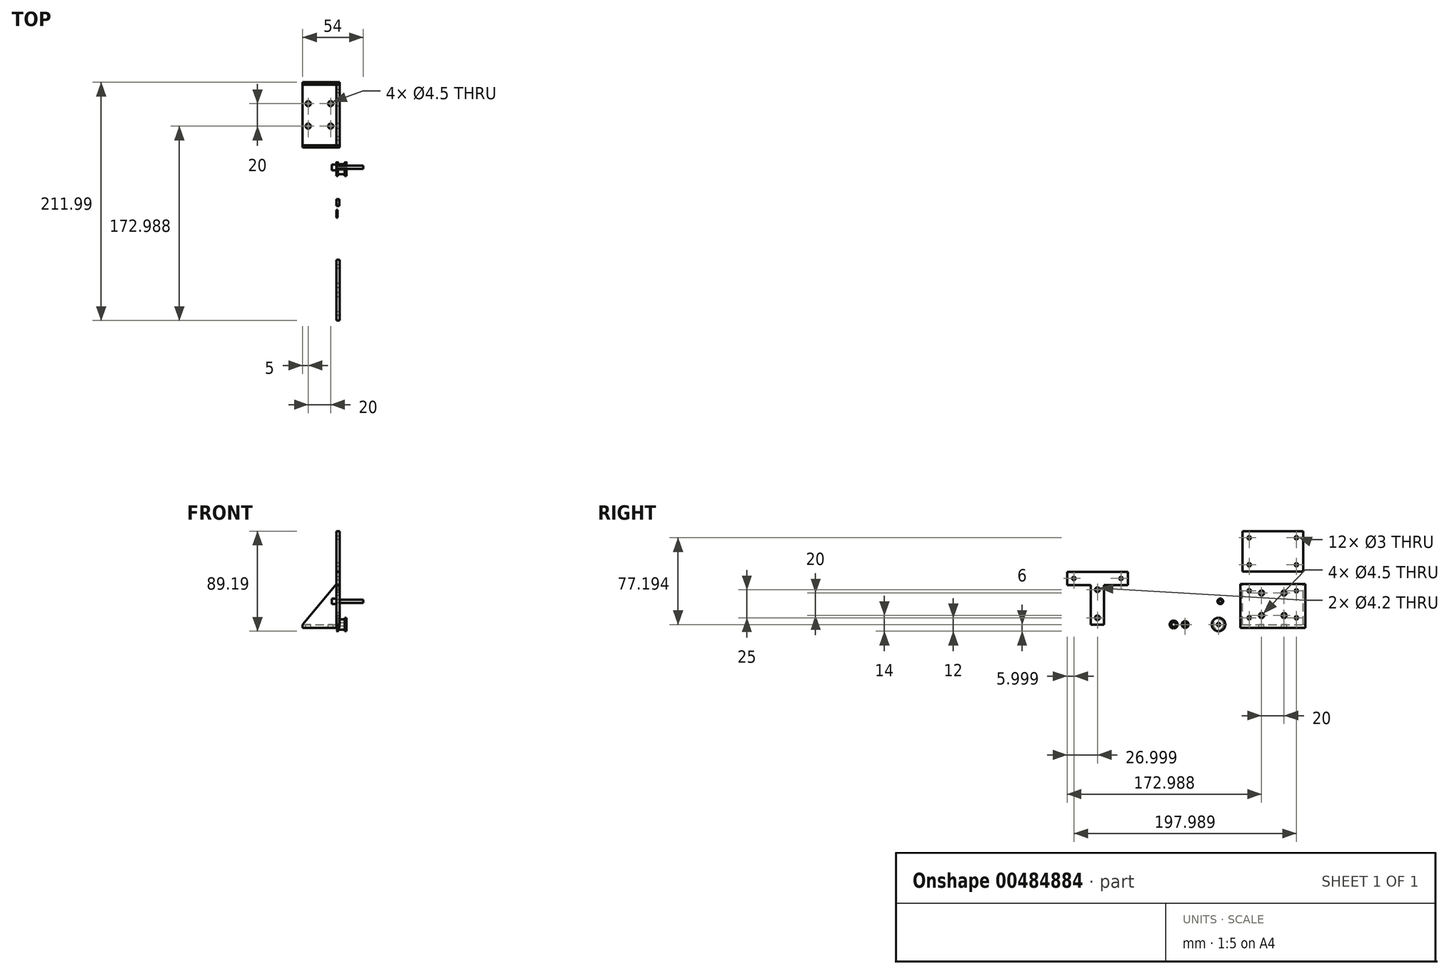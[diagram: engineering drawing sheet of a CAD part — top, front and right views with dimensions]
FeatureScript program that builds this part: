
annotation { "Feature Type Name" : "Feature", "Feature Type Description" : "" }
export const myFeature = defineFeature(function(context is Context, id is Id, definition is map)
    precondition{}
    {
        {
            var Q0;
            Q0=qCreatedBy(makeId("Right.planeOp"),FACE);
            var sketch = newSketch(context, id + "F0", { "sketchPlane" : qUnion([Q0])});
            skCircle(sketch, "E0", {"center": v(0, 0) * mm, "radius": 1.5 * mm});
            skCircle(sketch, "E1", {"center": v(0, 0) * mm, "radius": 4.5 * mm});
            skCircle(sketch, "E2", {"center": v(0, 0) * mm, "radius": 6 * mm});
            skSolve(sketch);
        }
        {
            var Q0;
            Q0=makeQuery(id+"F0.imprint","IMPRINT",FACE,{"disambiguationData":[TD([[makeQuery(id+"F0.imprint","IMPRINT",EDGE,{"derivedFrom":sQuery(id+"F0.wireOp",EDGE,"E0")}),1.0]])]});
            var Q1;
            Q1=makeQuery(id+"F0.imprint","IMPRINT",FACE,{"disambiguationData":[TD([[makeQuery(id+"F0.imprint","IMPRINT",EDGE,{"derivedFrom":sQuery(id+"F0.wireOp",EDGE,"E0")}),-1.0]])]});
            var Q2;
            Q2=makeQuery(id+"F0.imprint","IMPRINT",FACE,{"disambiguationData":[TD([[makeQuery(id+"F0.imprint","IMPRINT",EDGE,{"derivedFrom":sQuery(id+"F0.wireOp",EDGE,"E1")}),-1.0]])]});
            extrude(context, id + "F1", {"entities" : qUnion([Q0, Q1, Q2]), "depth" : 1.5 * mm, "offsetDistance" : 25 * mm});
        }
        {
            var Q0;
            Q0=makeQuery(id+"F0.imprint","IMPRINT",FACE,{"disambiguationData":[TD([[makeQuery(id+"F0.imprint","IMPRINT",EDGE,{"derivedFrom":sQuery(id+"F0.wireOp",EDGE,"E0")}),1.0]])]});
            var Q1;
            Q1=makeQuery(id+"F0.imprint","IMPRINT",FACE,{"disambiguationData":[TD([[makeQuery(id+"F0.imprint","IMPRINT",EDGE,{"derivedFrom":sQuery(id+"F0.wireOp",EDGE,"E0")}),-1.0]])]});
            extrude(context, id + "F2", {"entities" : qUnion([Q0, Q1]), "operationType" : NewBodyOperationType.ADD, "depth" : 7.5 * mm, "offsetDistance" : 25 * mm});
        }
        {
            var Q0;
            Q0=makeQuery(id+"F2.opExtrude","CAP_FACE",FACE,{"disambiguationData":[OSD([sQuery(id+"F0.wireOp",EDGE,"E1")])],"isStart":false});
            var sketch = newSketch(context, id + "F3", { "sketchPlane" : qUnion([Q0])});
            skCircle(sketch, "E3", {"center": v(0, 0) * mm, "radius": 6 * mm});
            skSolve(sketch);
        }
        {
            var Q0;
            Q0=makeQuery(id+"F3.imprint","IMPRINT",FACE,{"disambiguationData":[TD([[makeQuery(id+"F3.imprint","IMPRINT",EDGE,{"derivedFrom":makeQuery(id+"F2.opExtrude","CAP_EDGE",EDGE,{"disambiguationData":[OSD([sQuery(id+"F0.wireOp",EDGE,"E1")])],"isStart":false})}),1.0]])]});
            var Q1;
            Q1=makeQuery(id+"F3.imprint","IMPRINT",FACE,{"disambiguationData":[TD([[makeQuery(id+"F3.imprint","IMPRINT",EDGE,{"derivedFrom":sQuery(id+"F3.wireOp",EDGE,"E3")}),1.0]])]});
            extrude(context, id + "F4", {"entities" : qUnion([Q0, Q1]), "operationType" : NewBodyOperationType.ADD, "depth" : 1.5 * mm, "offsetDistance" : 25 * mm});
        }
        {
            var Q0;
            Q0=makeQuery(id+"F0.imprint","IMPRINT",FACE,{"disambiguationData":[TD([[makeQuery(id+"F0.imprint","IMPRINT",EDGE,{"derivedFrom":sQuery(id+"F0.wireOp",EDGE,"E0")}),1.0]])]});
            extrude(context, id + "F5", {"entities" : qUnion([Q0]), "operationType" : NewBodyOperationType.REMOVE, "endBound" : BoundingType.UP_TO_NEXT, "depth" : 25 * mm, "offsetDistance" : 25 * mm});
        }
        {
            var Q0;
            Q0=qCreatedBy(makeId("Right.planeOp"),FACE);
            var sketch = newSketch(context, id + "F6", { "sketchPlane" : qUnion([Q0])});
            skLineSegment(sketch, "E4.bottom", {"start": v(21.28, 0) * mm, "end": v(75.28, 0) * mm});
            skLineSegment(sketch, "E4.top", {"start": v(21.28, 36) * mm, "end": v(75.28, 36) * mm});
            skLineSegment(sketch, "E4.left", {"start": v(21.28, 0) * mm, "end": v(21.28, 36) * mm});
            skLineSegment(sketch, "E4.right", {"start": v(75.28, 0) * mm, "end": v(75.28, 36) * mm});
            skLineSegment(sketch, "E5", {"start": v(27.28, 0) * mm, "end": v(27.28, 6) * mm, "construction": true});
            skLineSegment(sketch, "E6", {"start": v(27.28, 6) * mm, "end": v(21.28, 6) * mm, "construction": true});
            skCircle(sketch, "E7", {"center": v(27.28, 6) * mm, "radius": 1.5 * mm});
            skLineSegment(sketch, "E8", {"start": v(27.28, 36) * mm, "end": v(27.28, 30) * mm, "construction": true});
            skLineSegment(sketch, "E9", {"start": v(27.28, 30) * mm, "end": v(21.28, 30) * mm, "construction": true});
            skLineSegment(sketch, "E10", {"start": v(69.28, 36) * mm, "end": v(69.28, 30) * mm, "construction": true});
            skLineSegment(sketch, "E11", {"start": v(69.28, 30) * mm, "end": v(75.28, 30) * mm, "construction": true});
            skLineSegment(sketch, "E12", {"start": v(75.28, 6) * mm, "end": v(69.28, 6) * mm, "construction": true});
            skLineSegment(sketch, "E13", {"start": v(69.28, 6) * mm, "end": v(69.28, 0) * mm, "construction": true});
            skCircle(sketch, "E14", {"center": v(69.28, 6) * mm, "radius": 1.5 * mm});
            skCircle(sketch, "E15", {"center": v(69.28, 30) * mm, "radius": 1.5 * mm});
            skCircle(sketch, "E16", {"center": v(27.28, 30) * mm, "radius": 1.5 * mm});
            skLineSegment(sketch, "E17", {"start": v(27.28, 30) * mm, "end": v(69.28, 30) * mm, "construction": true});
            skLineSegment(sketch, "E18", {"start": v(69.28, 30) * mm, "end": v(69.28, 6) * mm, "construction": true});
            skLineSegment(sketch, "E19", {"start": v(48.28, 36) * mm, "end": v(48.28, 0) * mm, "construction": true});
            skLineSegment(sketch, "E20", {"start": v(48.28, 18) * mm, "end": v(58.28, 18) * mm, "construction": true});
            skLineSegment(sketch, "E21", {"start": v(58.28, 18) * mm, "end": v(58.28, 28) * mm, "construction": true});
            skLineSegment(sketch, "E22", {"start": v(58.28, 18) * mm, "end": v(58.28, 8) * mm, "construction": true});
            skLineSegment(sketch, "E23", {"start": v(58.28, 28) * mm, "end": v(38.28, 28) * mm, "construction": true});
            skLineSegment(sketch, "E24", {"start": v(58.28, 8) * mm, "end": v(38.28, 8) * mm, "construction": true});
            skCircle(sketch, "E25", {"center": v(38.28, 28) * mm, "radius": 2.25 * mm});
            skCircle(sketch, "E26", {"center": v(58.28, 28) * mm, "radius": 2.25 * mm});
            skCircle(sketch, "E27", {"center": v(58.28, 8) * mm, "radius": 2.25 * mm});
            skCircle(sketch, "E28", {"center": v(38.28, 8) * mm, "radius": 2.25 * mm});
            skLineSegment(sketch, "E29", {"start": v(75.28, 36) * mm, "end": v(75.28, 47.2) * mm});
            skLineSegment(sketch, "E30.bottom", {"start": v(75.28, 47.2) * mm, "end": v(21.28, 47.2) * mm});
            skLineSegment(sketch, "E30.top", {"start": v(75.28, 83.2) * mm, "end": v(21.28, 83.2) * mm});
            skLineSegment(sketch, "E30.left", {"start": v(75.28, 47.2) * mm, "end": v(75.28, 83.2) * mm});
            skLineSegment(sketch, "E30.right", {"start": v(21.28, 47.2) * mm, "end": v(21.28, 83.2) * mm});
            skLineSegment(sketch, "E31", {"start": v(21.28, 53.2) * mm, "end": v(27.28, 53.2) * mm, "construction": true});
            skLineSegment(sketch, "E32", {"start": v(27.28, 53.2) * mm, "end": v(27.28, 47.2) * mm, "construction": true});
            skLineSegment(sketch, "E33", {"start": v(69.28, 47.2) * mm, "end": v(69.28, 53.2) * mm, "construction": true});
            skLineSegment(sketch, "E34", {"start": v(69.28, 53.2) * mm, "end": v(75.28, 53.2) * mm, "construction": true});
            skLineSegment(sketch, "E35", {"start": v(69.28, 83.2) * mm, "end": v(69.28, 77.2) * mm, "construction": true});
            skLineSegment(sketch, "E36", {"start": v(69.28, 77.2) * mm, "end": v(75.28, 77.2) * mm, "construction": true});
            skLineSegment(sketch, "E37", {"start": v(27.28, 83.2) * mm, "end": v(27.28, 77.2) * mm, "construction": true});
            skLineSegment(sketch, "E38", {"start": v(27.28, 77.2) * mm, "end": v(21.28, 77.2) * mm, "construction": true});
            skCircle(sketch, "E39", {"center": v(69.28, 77.2) * mm, "radius": 1.5 * mm});
            skCircle(sketch, "E40", {"center": v(69.28, 53.2) * mm, "radius": 1.5 * mm});
            skCircle(sketch, "E41", {"center": v(27.28, 53.2) * mm, "radius": 1.5 * mm});
            skCircle(sketch, "E42", {"center": v(27.28, 77.2) * mm, "radius": 1.5 * mm});
            skLineSegment(sketch, "E43", {"start": v(75.28, 0) * mm, "end": v(75.28, -3) * mm});
            skLineSegment(sketch, "E44", {"start": v(75.28, -3) * mm, "end": v(21.28, -3) * mm});
            skLineSegment(sketch, "E45", {"start": v(21.28, -3) * mm, "end": v(21.28, 0) * mm});
            skSolve(sketch);
        }
        {
            var Q0;
            {var subQ0=sQuery(id+"F6.wireOp",EDGE,"E4.bottom");Q0=makeQuery(id+"F6.imprint","IMPRINT",FACE,{"disambiguationData":[TD([[makeQuery(id+"F6.imprint","IMPRINT",EDGE,{"derivedFrom":subQ0}),1.0]])]});}
            var Q1;
            {var subQ0=sQuery(id+"F6.wireOp",EDGE,"E4.top");Q1=makeQuery(id+"F6.imprint","IMPRINT",FACE,{"disambiguationData":[TD([[makeQuery(id+"F6.imprint","IMPRINT",EDGE,{"derivedFrom":subQ0}),-1.0]])]});}
            var Q2;
            Q2=makeQuery(id+"F6.imprint","IMPRINT",FACE,{"disambiguationData":[TD([[makeQuery(id+"F6.imprint","IMPRINT",EDGE,{"derivedFrom":sQuery(id+"F6.wireOp",EDGE,"E4.bottom")}),-1.0]])]});
            extrude(context, id + "F7", {"entities" : qUnion([Q0, Q1, Q2]), "depth" : 3 * mm, "offsetDistance" : 25 * mm});
        }
        {
            var Q0;
            Q0=qCreatedBy(makeId("Right.planeOp"),FACE);
            var sketch = newSketch(context, id + "F8", { "sketchPlane" : qUnion([Q0])});
            skCircle(sketch, "E46", {"center": v(1.57, 20.62) * mm, "radius": 1.5 * mm});
            skCircle(sketch, "E47", {"center": v(1.57, 20.62) * mm, "radius": 2.5 * mm});
            skSolve(sketch);
        }
        {
            var Q0;
            Q0=makeQuery(id+"F8.imprint","IMPRINT",FACE,{"disambiguationData":[TD([[makeQuery(id+"F8.imprint","IMPRINT",EDGE,{"derivedFrom":sQuery(id+"F8.wireOp",EDGE,"E46")}),1.0]])]});
            extrude(context, id + "F9", {"entities" : qUnion([Q0]), "depth" : 24 * mm, "offsetDistance" : 25 * mm});
        }
        {
            var Q0;
            Q0=makeQuery(id+"F8.imprint","IMPRINT",FACE,{"disambiguationData":[TD([[makeQuery(id+"F8.imprint","IMPRINT",EDGE,{"derivedFrom":sQuery(id+"F8.wireOp",EDGE,"E46")}),-1.0]])]});
            var Q1;
            Q1=makeQuery(id+"F8.imprint","IMPRINT",FACE,{"disambiguationData":[TD([[makeQuery(id+"F8.imprint","IMPRINT",EDGE,{"derivedFrom":sQuery(id+"F8.wireOp",EDGE,"E46")}),1.0]])]});
            extrude(context, id + "F10", {"entities" : qUnion([Q0, Q1]), "operationType" : NewBodyOperationType.ADD, "oppositeDirection" : true, "depth" : 4 * mm, "offsetDistance" : 25 * mm});
        }
        {
            var Q0;
            Q0=qCreatedBy(makeId("Right.planeOp"),FACE);
            var sketch = newSketch(context, id + "F11", { "sketchPlane" : qUnion([Q0])});
            skCircle(sketch, "E48", {"center": v(-29.72, 0) * mm, "radius": 1.5 * mm});
            skCircle(sketch, "E49", {"center": v(-29.72, 0) * mm, "radius": 3 * mm});
            skCircle(sketch, "E50", {"center": v(-39.93, 0) * mm, "radius": 2 * mm});
            skCircle(sketch, "E51", {"center": v(-39.93, 0) * mm, "radius": 3.5 * mm});
            skSolve(sketch);
        }
        {
            var Q0;
            Q0=makeQuery(id+"F11.imprint","IMPRINT",FACE,{"disambiguationData":[TD([[makeQuery(id+"F11.imprint","IMPRINT",EDGE,{"derivedFrom":sQuery(id+"F11.wireOp",EDGE,"E48")}),-1.0]])]});
            extrude(context, id + "F12", {"entities" : qUnion([Q0]), "depth" : 2.5 * mm, "offsetDistance" : 25 * mm});
        }
        {
            var Q0;
            Q0=makeQuery(id+"F6.imprint","IMPRINT",FACE,{"disambiguationData":[TD([[makeQuery(id+"F6.imprint","IMPRINT",EDGE,{"derivedFrom":sQuery(id+"F6.wireOp",EDGE,"E30.bottom")}),-1.0]])]});
            extrude(context, id + "F13", {"entities" : qUnion([Q0]), "depth" : 3 * mm, "offsetDistance" : 25 * mm});
        }
        {
            var Q0;
            Q0=makeQuery(id+"F6.imprint","IMPRINT",FACE,{"disambiguationData":[TD([[makeQuery(id+"F6.imprint","IMPRINT",EDGE,{"derivedFrom":sQuery(id+"F6.wireOp",EDGE,"E4.bottom")}),-1.0]])]});
            extrude(context, id + "F14", {"entities" : qUnion([Q0]), "operationType" : NewBodyOperationType.ADD, "oppositeDirection" : true, "depth" : 30 * mm, "offsetDistance" : 25 * mm});
        }
        {
            var Q0;
            Q0=makeQuery(id+"F14.opExtrude","SWEPT_FACE",FACE,{"disambiguationData":[OSD([sQuery(id+"F6.wireOp",EDGE,"E4.bottom")])]});
            var sketch = newSketch(context, id + "F15", { "sketchPlane" : qUnion([Q0])});
            skLineSegment(sketch, "E52", {"start": v(-15, 21.28) * mm, "end": v(-15, 75.28) * mm});
            skLineSegment(sketch, "E53.bottom", {"start": v(-25, 58.28) * mm, "end": v(-5, 58.28) * mm, "construction": true});
            skLineSegment(sketch, "E53.top", {"start": v(-25, 38.28) * mm, "end": v(-5, 38.28) * mm, "construction": true});
            skLineSegment(sketch, "E53.left", {"start": v(-25, 58.28) * mm, "end": v(-25, 38.28) * mm, "construction": true});
            skLineSegment(sketch, "E53.right", {"start": v(-5, 58.28) * mm, "end": v(-5, 38.28) * mm, "construction": true});
            skPoint(sketch, "E53.middle", {"position": v(-15, 48.28) * mm});
            skCircle(sketch, "E54", {"center": v(-5, 38.28) * mm, "radius": 2.25 * mm});
            skCircle(sketch, "E55", {"center": v(-25, 38.28) * mm, "radius": 2.25 * mm});
            skCircle(sketch, "E56", {"center": v(-25, 58.28) * mm, "radius": 2.25 * mm});
            skCircle(sketch, "E57", {"center": v(-5, 58.28) * mm, "radius": 2.25 * mm});
            skSolve(sketch);
        }
        {
            var Q0;
            Q0=makeQuery(id+"F15.imprint","IMPRINT",FACE,{"disambiguationData":[TD([[makeQuery(id+"F15.imprint","IMPRINT",EDGE,{"derivedFrom":sQuery(id+"F15.wireOp",EDGE,"E55")}),1.0]])]});
            var Q1;
            Q1=makeQuery(id+"F15.imprint","IMPRINT",FACE,{"disambiguationData":[TD([[makeQuery(id+"F15.imprint","IMPRINT",EDGE,{"derivedFrom":sQuery(id+"F15.wireOp",EDGE,"E54")}),1.0]])]});
            var Q2;
            Q2=makeQuery(id+"F15.imprint","IMPRINT",FACE,{"disambiguationData":[TD([[makeQuery(id+"F15.imprint","IMPRINT",EDGE,{"derivedFrom":sQuery(id+"F15.wireOp",EDGE,"E57")}),1.0]])]});
            var Q3;
            Q3=makeQuery(id+"F15.imprint","IMPRINT",FACE,{"disambiguationData":[TD([[makeQuery(id+"F15.imprint","IMPRINT",EDGE,{"derivedFrom":sQuery(id+"F15.wireOp",EDGE,"E56")}),1.0]])]});
            extrude(context, id + "F16", {"entities" : qUnion([Q0, Q1, Q2, Q3]), "operationType" : NewBodyOperationType.REMOVE, "endBound" : BoundingType.UP_TO_NEXT, "oppositeDirection" : true, "depth" : 25 * mm, "offsetDistance" : 25 * mm});
        }
        {
            var Q0;
            {var subQ0=sQuery(id+"F6.wireOp",EDGE,"E43");Q0=makeQuery(id+"F14.boolean.opBoolean","MERGE",FACE,{"derivedFrom":[makeQuery(id+"F7.opExtrude","SWEPT_FACE",FACE,{"disambiguationData":[OSD([sQuery(id+"F6.wireOp",EDGE,"E4.right"),subQ0])]}),makeQuery(id+"F14.opExtrude","SWEPT_FACE",FACE,{"disambiguationData":[OSD([subQ0])]})]});}
            var sketch = newSketch(context, id + "F17", { "sketchPlane" : qUnion([Q0])});
            skLineSegment(sketch, "E58", {"start": v(0, 36) * mm, "end": v(30, 0) * mm});
            skLineSegment(sketch, "E59", {"start": v(30, 0) * mm, "end": v(30, -3) * mm});
            skLineSegment(sketch, "E60", {"start": v(30, -3) * mm, "end": v(-3, -3) * mm});
            skLineSegment(sketch, "E61", {"start": v(-3, -3) * mm, "end": v(-3, 36) * mm});
            skLineSegment(sketch, "E62", {"start": v(-3, 36) * mm, "end": v(0, 36) * mm});
            skSolve(sketch);
        }
        {
            var Q0;
            Q0=makeQuery(id+"F17.imprint","IMPRINT",FACE,{"disambiguationData":[TD([[makeQuery(id+"F17.imprint","IMPRINT",EDGE,{"derivedFrom":sQuery(id+"F17.wireOp",EDGE,"E58")}),-1.0]])]});
            var Q1;
            Q1=makeQuery(id+"F17.imprint","IMPRINT",FACE,{"disambiguationData":[TD([[makeQuery(id+"F17.imprint","IMPRINT",EDGE,{"derivedFrom":sQuery(id+"F17.wireOp",EDGE,"E59")}),-1.0]])]});
            extrude(context, id + "F18", {"entities" : qUnion([Q0, Q1]), "operationType" : NewBodyOperationType.ADD, "depth" : 2 * mm, "offsetDistance" : 25 * mm});
        }
        {
            var Q0;
            {var subQ0=sQuery(id+"F6.wireOp",EDGE,"E45");Q0=makeQuery(id+"F14.boolean.opBoolean","MERGE",FACE,{"derivedFrom":[makeQuery(id+"F7.opExtrude","SWEPT_FACE",FACE,{"disambiguationData":[OSD([sQuery(id+"F6.wireOp",EDGE,"E4.left"),subQ0])]}),makeQuery(id+"F14.opExtrude","SWEPT_FACE",FACE,{"disambiguationData":[OSD([subQ0])]})]});}
            var sketch = newSketch(context, id + "F19", { "sketchPlane" : qUnion([Q0])});
            skLineSegment(sketch, "E63", {"start": v(0, 36) * mm, "end": v(-30, 0) * mm});
            skLineSegment(sketch, "E64", {"start": v(-30, 0) * mm, "end": v(-30, -3) * mm});
            skLineSegment(sketch, "E65", {"start": v(-30, -3) * mm, "end": v(3, -3) * mm});
            skLineSegment(sketch, "E66", {"start": v(3, -3) * mm, "end": v(3, 36) * mm});
            skLineSegment(sketch, "E67", {"start": v(3, 36) * mm, "end": v(0, 36) * mm});
            skSolve(sketch);
        }
        {
            var Q0;
            Q0=makeQuery(id+"F19.imprint","IMPRINT",FACE,{"disambiguationData":[TD([[makeQuery(id+"F19.imprint","IMPRINT",EDGE,{"derivedFrom":sQuery(id+"F19.wireOp",EDGE,"E63")}),1.0]])]});
            var Q1;
            Q1=makeQuery(id+"F19.imprint","IMPRINT",FACE,{"disambiguationData":[TD([[makeQuery(id+"F19.imprint","IMPRINT",EDGE,{"derivedFrom":sQuery(id+"F19.wireOp",EDGE,"E64")}),-1.0]])]});
            extrude(context, id + "F20", {"entities" : qUnion([Q0, Q1]), "operationType" : NewBodyOperationType.ADD, "depth" : 2 * mm, "offsetDistance" : 25 * mm});
        }
        {
            var Q0;
            Q0=qCreatedBy(makeId("Right.planeOp"),FACE);
            var sketch = newSketch(context, id + "F21", { "sketchPlane" : qUnion([Q0])});
            skLineSegment(sketch, "E68", {"start": v(-101.71, 0) * mm, "end": v(-113.71, 0) * mm});
            skLineSegment(sketch, "E69", {"start": v(-113.71, 0) * mm, "end": v(-113.71, 35) * mm});
            skLineSegment(sketch, "E70", {"start": v(-113.71, 35) * mm, "end": v(-134.71, 35) * mm});
            skLineSegment(sketch, "E71", {"start": v(-134.71, 35) * mm, "end": v(-134.71, 47) * mm});
            skLineSegment(sketch, "E72", {"start": v(-101.71, 0) * mm, "end": v(-101.71, 35) * mm});
            skLineSegment(sketch, "E73", {"start": v(-101.71, 35) * mm, "end": v(-80.71, 35) * mm});
            skLineSegment(sketch, "E74", {"start": v(-80.71, 35) * mm, "end": v(-80.71, 47) * mm});
            skLineSegment(sketch, "E75", {"start": v(-134.71, 47) * mm, "end": v(-80.71, 47) * mm});
            skLineSegment(sketch, "E76", {"start": v(-134.71, 41) * mm, "end": v(-128.71, 41) * mm, "construction": true});
            skLineSegment(sketch, "E77", {"start": v(-80.71, 41) * mm, "end": v(-86.71, 41) * mm, "construction": true});
            skCircle(sketch, "E78", {"center": v(-128.71, 41) * mm, "radius": 1.5 * mm});
            skCircle(sketch, "E79", {"center": v(-86.71, 41) * mm, "radius": 1.5 * mm});
            skLineSegment(sketch, "E80", {"start": v(-107.71, 0) * mm, "end": v(-107.71, 6) * mm, "construction": true});
            skLineSegment(sketch, "E81", {"start": v(-113.71, 35) * mm, "end": v(-101.71, 35) * mm, "construction": true});
            skCircle(sketch, "E82", {"center": v(-107.71, 6) * mm, "radius": 2.1 * mm});
            skLineSegment(sketch, "E83", {"start": v(-107.71, 6) * mm, "end": v(-107.71, 31) * mm, "construction": true});
            skCircle(sketch, "E84", {"center": v(-107.71, 31) * mm, "radius": 2.1 * mm});
            skSolve(sketch);
        }
        {
            var Q0;
            Q0=makeQuery(id+"F21.imprint","IMPRINT",FACE,{"disambiguationData":[TD([[makeQuery(id+"F21.imprint","IMPRINT",EDGE,{"derivedFrom":sQuery(id+"F21.wireOp",EDGE,"E68")}),-1.0]])]});
            extrude(context, id + "F22", {"entities" : qUnion([Q0]), "depth" : 3 * mm, "offsetDistance" : 25 * mm});
        }
        {
            var Q0;
            Q0=makeQuery(id+"F11.imprint","IMPRINT",FACE,{"disambiguationData":[TD([[makeQuery(id+"F11.imprint","IMPRINT",EDGE,{"derivedFrom":sQuery(id+"F11.wireOp",EDGE,"E50")}),-1.0]])]});
            extrude(context, id + "F23", {"entities" : qUnion([Q0]), "depth" : 1 * mm, "offsetDistance" : 25 * mm});
        }
    });
